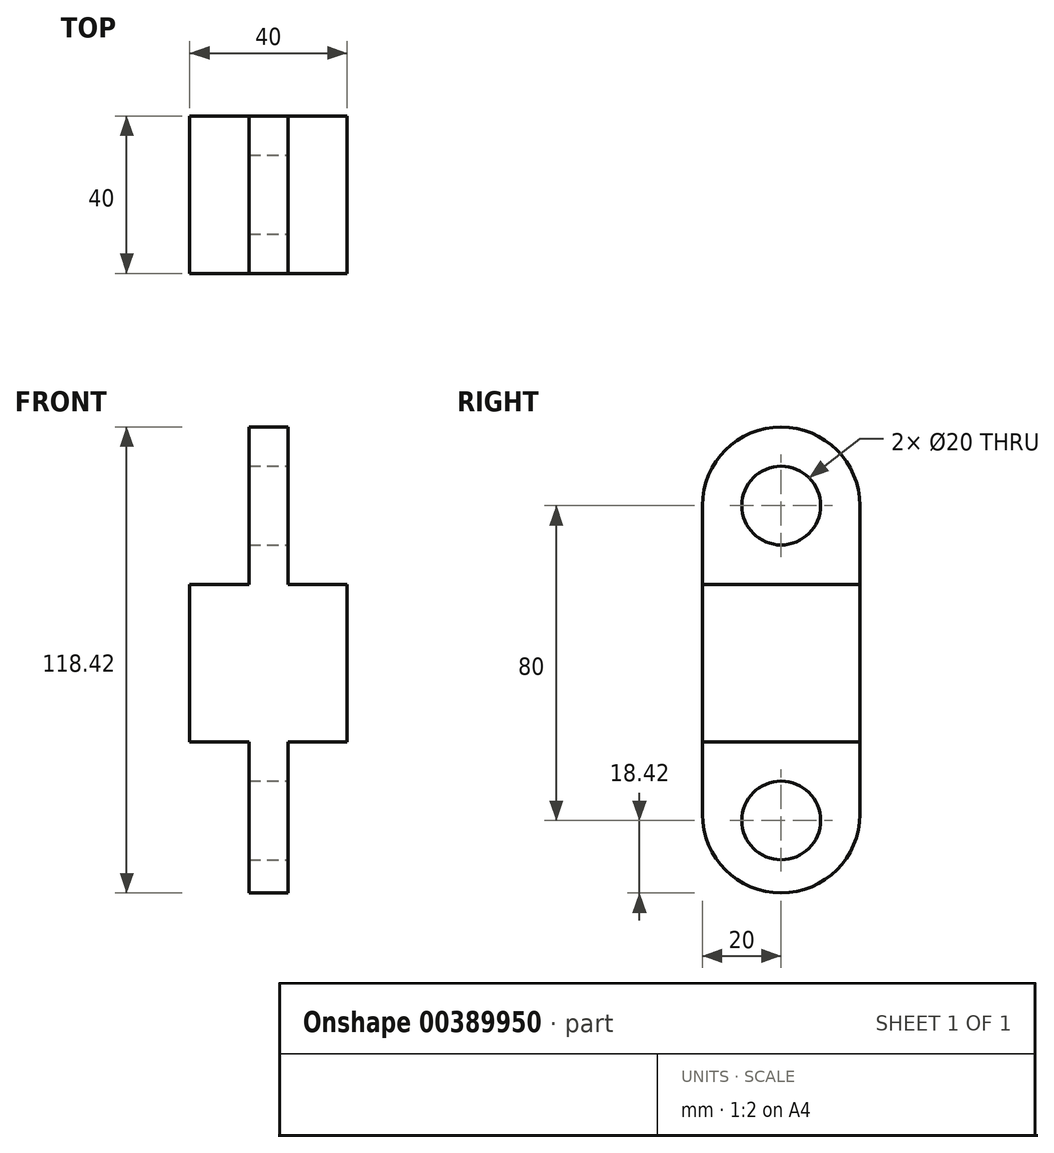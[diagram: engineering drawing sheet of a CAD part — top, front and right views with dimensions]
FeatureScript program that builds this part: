
annotation { "Feature Type Name" : "Feature", "Feature Type Description" : "" }
export const myFeature = defineFeature(function(context is Context, id is Id, definition is map)
    precondition{}
    {
        {
            var Q0;
            Q0=qCreatedBy(makeId("Top.planeOp"),FACE);
            var sketch = newSketch(context, id + "F0", { "sketchPlane" : qUnion([Q0])});
            skLineSegment(sketch, "E0.bottom", {"start": v(20, -20) * mm, "end": v(-20, -20) * mm});
            skLineSegment(sketch, "E0.top", {"start": v(20, 20) * mm, "end": v(-20, 20) * mm});
            skLineSegment(sketch, "E0.left", {"start": v(20, -20) * mm, "end": v(20, 20) * mm});
            skLineSegment(sketch, "E0.right", {"start": v(-20, -20) * mm, "end": v(-20, 20) * mm});
            skPoint(sketch, "E0.middle", {"position": v(0, 0) * mm});
            skSolve(sketch);
        }
        {
            var Q0;
            Q0 = qSketchRegion(id + "F0", true);
            extrude(context, id + "F1", {"entities" : qUnion([Q0]), "depth" : 40 * mm});
        }
        {
            var Q0;
            Q0=qCreatedBy(makeId("Right.planeOp"),FACE);
            var sketch = newSketch(context, id + "F2", { "sketchPlane" : qUnion([Q0])});
            skLineSegment(sketch, "E1.top", {"start": v(-20, 40) * mm, "end": v(20, 40) * mm});
            skLineSegment(sketch, "E1.left", {"start": v(-20, 60) * mm, "end": v(-20, 40) * mm});
            skLineSegment(sketch, "E1.right", {"start": v(20, 60) * mm, "end": v(20, 40) * mm});
            skArc(sketch, "E2", {"start": v(20, 60) * mm, "mid": v(0, 80) * mm, "end": v(-20, 60) * mm});
            skLineSegment(sketch, "E3.top", {"start": v(20, 0) * mm, "end": v(-20, 0) * mm});
            skLineSegment(sketch, "E3.left", {"start": v(20, -18.42) * mm, "end": v(20, 0) * mm});
            skLineSegment(sketch, "E3.right", {"start": v(-20, -18.42) * mm, "end": v(-20, 0) * mm});
            skArc(sketch, "E4", {"start": v(-20, -18.42) * mm, "mid": v(0, -38.42) * mm, "end": v(20, -18.42) * mm});
            skSolve(sketch);
        }
        {
            var Q0;
            Q0 = qSketchRegion(id + "F2", true);
            extrude(context, id + "F3", {"entities" : qUnion([Q0]), "operationType" : NewBodyOperationType.ADD, "endBound" : BoundingType.SYMMETRIC, "depth" : 10 * mm});
        }
        {
            var Q0;
            Q0=makeQuery(id+"F3.opExtrude","CAP_FACE",FACE,{"disambiguationData":[OSD([sQuery(id+"F2.wireOp",EDGE,"E1.top"),sQuery(id+"F2.wireOp",EDGE,"E1.left"),sQuery(id+"F2.wireOp",EDGE,"E1.right"),sQuery(id+"F2.wireOp",EDGE,"E2")])],"isStart":false});
            var sketch = newSketch(context, id + "F4", { "sketchPlane" : qUnion([Q0])});
            skLineSegment(sketch, "E5", {"start": v(0, 60) * mm, "end": v(0, 40) * mm, "construction": true});
            skCircle(sketch, "E6", {"center": v(0, 60) * mm, "radius": 10 * mm});
            skLineSegment(sketch, "E7", {"start": v(0, 0) * mm, "end": v(0, -20) * mm, "construction": true});
            skCircle(sketch, "E8", {"center": v(0, -20) * mm, "radius": 10 * mm});
            skSolve(sketch);
        }
        {
            var Q0;
            Q0 = qSketchRegion(id + "F4", true);
            extrude(context, id + "F5", {"entities" : qUnion([Q0]), "operationType" : NewBodyOperationType.REMOVE, "oppositeDirection" : true, "depth" : 25 * mm});
        }
    });
